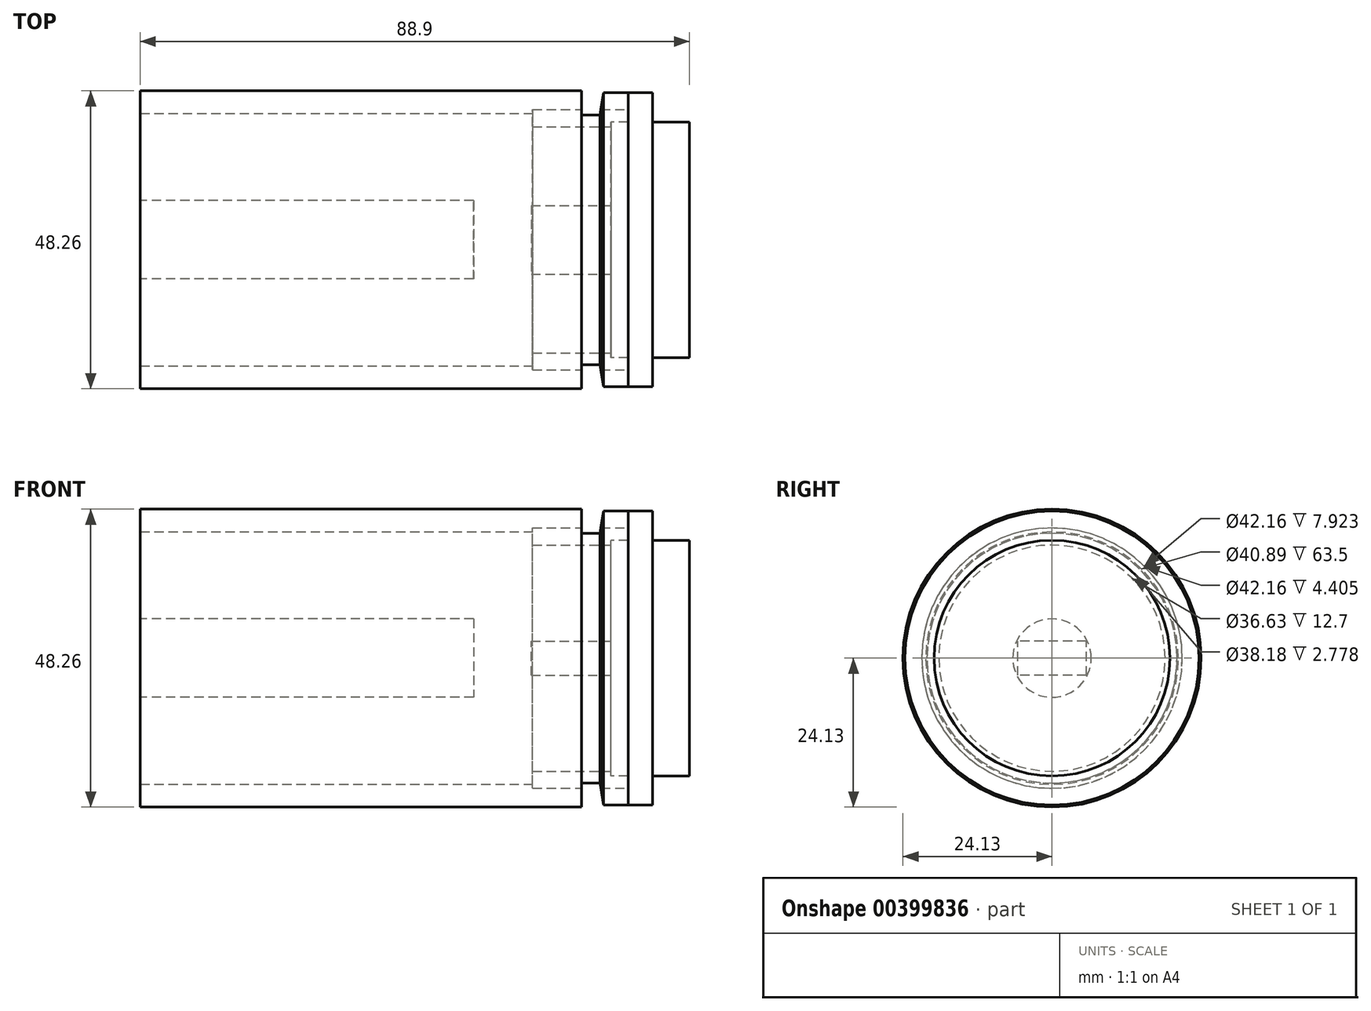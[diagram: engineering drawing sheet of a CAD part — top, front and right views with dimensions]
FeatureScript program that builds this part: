
annotation { "Feature Type Name" : "Feature", "Feature Type Description" : "" }
export const myFeature = defineFeature(function(context is Context, id is Id, definition is map)
    precondition{}
    {
        {
            var Q0;
            Q0=qCreatedBy(makeId("Right.planeOp"),FACE);
            var sketch = newSketch(context, id + "F0", { "sketchPlane" : qUnion([Q0])});
            skCircle(sketch, "E0", {"center": v(0, 0) * mm, "radius": 22.62 * mm});
            skCircle(sketch, "E1", {"center": v(0, 0) * mm, "radius": 23.81 * mm});
            skLineSegment(sketch, "E2.bottom", {"start": v(5.56, -2.78) * mm, "end": v(-5.56, -2.78) * mm});
            skLineSegment(sketch, "E2.top", {"start": v(5.56, 2.78) * mm, "end": v(-5.56, 2.78) * mm});
            skLineSegment(sketch, "E2.left", {"start": v(5.56, -2.78) * mm, "end": v(5.56, 2.78) * mm});
            skLineSegment(sketch, "E2.right", {"start": v(-5.56, -2.78) * mm, "end": v(-5.56, 2.78) * mm});
            skCircle(sketch, "E3", {"center": v(0, 0) * mm, "radius": 19.09 * mm});
            skSolve(sketch);
        }
        {
            var Q0;
            Q0=qCreatedBy(makeId("Right.planeOp"),FACE);
            var sketch = newSketch(context, id + "F1", { "sketchPlane" : qUnion([Q0])});
            skCircle(sketch, "E4", {"center": v(0, 0) * mm, "radius": 18.31 * mm});
            skCircle(sketch, "E5", {"center": v(0, 0) * mm, "radius": 21.08 * mm});
            skCircle(sketch, "E6", {"center": v(0, 0) * mm, "radius": 20.45 * mm});
            skCircle(sketch, "E7", {"center": v(0, 0) * mm, "radius": 24.13 * mm});
            skSolve(sketch);
        }
        {
            var Q0;
            Q0=makeQuery(id+"F0.imprint","IMPRINT",FACE,{"disambiguationData":[TD([[makeQuery(id+"F0.imprint","IMPRINT",EDGE,{"derivedFrom":sQuery(id+"F0.wireOp",EDGE,"E2.bottom")}),-1.0]])]});
            extrude(context, id + "F2", {"entities" : qUnion([Q0]), "oppositeDirection" : true, "depth" : 12.9 * mm, "offsetDistance" : 25.4 * mm});
        }
        {
            var Q0;
            Q0=makeQuery(id+"F0.imprint","IMPRINT",FACE,{"disambiguationData":[TD([[makeQuery(id+"F0.imprint","IMPRINT",EDGE,{"derivedFrom":sQuery(id+"F0.wireOp",EDGE,"E2.bottom")}),1.0]])]});
            var Q1;
            Q1=makeQuery(id+"F0.imprint","IMPRINT",FACE,{"disambiguationData":[TD([[makeQuery(id+"F0.imprint","IMPRINT",EDGE,{"derivedFrom":sQuery(id+"F0.wireOp",EDGE,"E2.bottom")}),-1.0]])]});
            extrude(context, id + "F3", {"entities" : qUnion([Q0, Q1]), "operationType" : NewBodyOperationType.ADD, "depth" : 12.7 * mm, "offsetDistance" : 25.4 * mm});
        }
        {
            var Q0;
            Q0=makeQuery(id+"F0.imprint","IMPRINT",FACE,{"disambiguationData":[TD([[makeQuery(id+"F0.imprint","IMPRINT",EDGE,{"derivedFrom":sQuery(id+"F0.wireOp",EDGE,"E2.bottom")}),-1.0]])]});
            var Q1;
            Q1=makeQuery(id+"F0.imprint","IMPRINT",FACE,{"disambiguationData":[TD([[makeQuery(id+"F0.imprint","IMPRINT",EDGE,{"derivedFrom":sQuery(id+"F0.wireOp",EDGE,"E0")}),1.0]])]});
            var Q2;
            Q2=makeQuery(id+"F0.imprint","IMPRINT",FACE,{"disambiguationData":[TD([[makeQuery(id+"F0.imprint","IMPRINT",EDGE,{"derivedFrom":sQuery(id+"F0.wireOp",EDGE,"E0")}),-1.0]])]});
            var Q3;
            Q3=makeQuery(id+"F0.imprint","IMPRINT",FACE,{"disambiguationData":[TD([[makeQuery(id+"F0.imprint","IMPRINT",EDGE,{"derivedFrom":sQuery(id+"F0.wireOp",EDGE,"E1")}),1.0]])]});
            extrude(context, id + "F4", {"entities" : qUnion([Q0, Q1, Q2, Q3]), "operationType" : NewBodyOperationType.ADD, "depth" : 6.75 * mm, "offsetDistance" : 25.4 * mm, "hasSecondDirection" : true, "secondDirectionOppositeDirection" : false, "secondDirectionDepth" : 2.78 * mm});
        }
        {
            var Q0;
            Q0=makeQuery(id+"F1.imprint","IMPRINT",FACE,{"disambiguationData":[TD([[makeQuery(id+"F1.imprint","IMPRINT",EDGE,{"derivedFrom":sQuery(id+"F1.wireOp",EDGE,"E5")}),-1.0]])]});
            var Q1;
            Q1=makeQuery(id+"F1.imprint","IMPRINT",FACE,{"disambiguationData":[TD([[makeQuery(id+"F1.imprint","IMPRINT",EDGE,{"derivedFrom":sQuery(id+"F1.wireOp",EDGE,"E5")}),1.0]])]});
            var Q2;
            Q2=makeQuery(id+"F4.opExtrude","CAP_FACE",FACE,{"disambiguationData":[OSD([sQuery(id+"F0.wireOp",EDGE,"E1"),sQuery(id+"F0.wireOp",EDGE,"E3")])],"isStart":true});
            extrude(context, id + "F5", {"entities" : qUnion([Q0, Q1]), "oppositeDirection" : true, "depth" : 76.2 * mm, "offsetDistance" : 25.4 * mm, "hasSecondDirection" : true, "secondDirectionBound" : SecondDirectionBoundingType.UP_TO_SURFACE, "secondDirectionOppositeDirection" : false, "secondDirectionDepth" : 5.08 * mm, "secondDirectionBoundEntityFace" : qUnion([Q2])});
        }
        {
            var Q0;
            Q0=makeQuery(id+"F1.imprint","IMPRINT",FACE,{"disambiguationData":[TD([[makeQuery(id+"F1.imprint","IMPRINT",EDGE,{"derivedFrom":sQuery(id+"F1.wireOp",EDGE,"E4")}),-1.0]])]});
            var Q1;
            Q1=makeQuery(id+"F1.imprint","IMPRINT",FACE,{"disambiguationData":[TD([[makeQuery(id+"F1.imprint","IMPRINT",EDGE,{"derivedFrom":sQuery(id+"F1.wireOp",EDGE,"E5")}),1.0]])]});
            var Q2;
            Q2=makeQuery(id+"F4.opExtrude","CAP_FACE",FACE,{"disambiguationData":[OSD([sQuery(id+"F0.wireOp",EDGE,"E1"),sQuery(id+"F0.wireOp",EDGE,"E3")])],"isStart":true});
            extrude(context, id + "F6", {"entities" : qUnion([Q0, Q1]), "oppositeDirection" : true, "depth" : 12.7 * mm, "offsetDistance" : 25.4 * mm, "hasSecondDirection" : true, "secondDirectionBound" : SecondDirectionBoundingType.UP_TO_SURFACE, "secondDirectionOppositeDirection" : false, "secondDirectionDepth" : 25.4 * mm, "secondDirectionBoundEntityFace" : qUnion([Q2])});
        }
        {
            var Q0;
            Q0=makeQuery(id+"F6.opExtrude","SWEPT_BODY",BODY,{"disambiguationData":[OSD([sQuery(id+"F1.wireOp",EDGE,"E4"),sQuery(id+"F1.wireOp",EDGE,"E5")])]});
            var Q1;
            Q1=makeQuery(id+"F5.opExtrude","SWEPT_BODY",BODY,{"disambiguationData":[OSD([sQuery(id+"F1.wireOp",EDGE,"E6"),sQuery(id+"F1.wireOp",EDGE,"E7")])]});
            booleanBodies(context, id + "F7", {"operationType" : BooleanOperationType.SUBTRACTION, "tools" : qUnion([Q0]), "targets" : qUnion([Q1]), "keepTools" : true});
        }
        {
            var Q0;
            Q0=qCreatedBy(makeId("Front.planeOp"),FACE);
            var sketch = newSketch(context, id + "F8", { "sketchPlane" : qUnion([Q0])});
            skLineSegment(sketch, "E8", {"start": v(6.75, 23.81) * mm, "end": v(-1.2, 23.81) * mm, "construction": true});
            skLineSegment(sketch, "E9", {"start": v(2.78, 23.81) * mm, "end": v(-1.2, 23.81) * mm});
            skLineSegment(sketch, "E10", {"start": v(-1.2, 23.81) * mm, "end": v(-1.76, 20.24) * mm});
            skLineSegment(sketch, "E11", {"start": v(-1.76, 20.24) * mm, "end": v(-4.78, 20.24) * mm});
            skLineSegment(sketch, "E12", {"start": v(-4.78, 20.24) * mm, "end": v(-4.78, 26.6) * mm});
            skLineSegment(sketch, "E13", {"start": v(-4.78, 26.6) * mm, "end": v(2.78, 26.6) * mm});
            skLineSegment(sketch, "E14", {"start": v(2.78, 26.6) * mm, "end": v(2.78, 23.81) * mm});
            skLineSegment(sketch, "E15", {"start": v(16.52, 0) * mm, "end": v(-15.37, 0) * mm, "construction": true});
            skSolve(sketch);
        }
        {
            var Q0;
            Q0 = qSketchRegion(id + "F8", true);
            var Q1;
            Q1=sQuery(id+"F8.wireOp",EDGE,"E15");
            revolve(context, id + "F9", {"operationType" : NewBodyOperationType.REMOVE, "entities" : qUnion([Q0]), "axis" : qUnion([Q1]), "revolveType" : RevolveType.FULL, "oppositeDirection" : true});
        }
        {
            var Q0;
            Q0=makeQuery(id+"F2.opExtrude","SWEPT_BODY",BODY,{"disambiguationData":[OSD([sQuery(id+"F0.wireOp",EDGE,"E2.bottom"),sQuery(id+"F0.wireOp",EDGE,"E2.top"),sQuery(id+"F0.wireOp",EDGE,"E2.left"),sQuery(id+"F0.wireOp",EDGE,"E2.right")])]});
            var Q1;
            Q1=makeQuery(id+"F6.opExtrude","SWEPT_BODY",BODY,{"disambiguationData":[OSD([sQuery(id+"F1.wireOp",EDGE,"E4"),sQuery(id+"F1.wireOp",EDGE,"E5")])]});
            booleanBodies(context, id + "F10", {"operationType" : BooleanOperationType.SUBTRACTION, "tools" : qUnion([Q0]), "targets" : qUnion([Q1]), "keepTools" : true});
        }
        {
            var Q0;
            Q0=makeQuery(id+"F5.opExtrude","CAP_FACE",FACE,{"disambiguationData":[OSD([sQuery(id+"F1.wireOp",EDGE,"E6"),sQuery(id+"F1.wireOp",EDGE,"E7")])],"isStart":false});
            var sketch = newSketch(context, id + "F11", { "sketchPlane" : qUnion([Q0])});
            skCircle(sketch, "E16", {"center": v(0, 0) * mm, "radius": 6.35 * mm});
            skSolve(sketch);
        }
        {
            var Q0;
            Q0=makeQuery(id+"F11.imprint","IMPRINT",FACE,{"disambiguationData":[TD([[makeQuery(id+"F11.imprint","IMPRINT",EDGE,{"derivedFrom":sQuery(id+"F11.wireOp",EDGE,"E16")}),1.0]])]});
            extrude(context, id + "F12", {"entities" : qUnion([Q0]), "oppositeDirection" : true, "depth" : 53.97 * mm, "offsetDistance" : 25.4 * mm});
        }
    });
